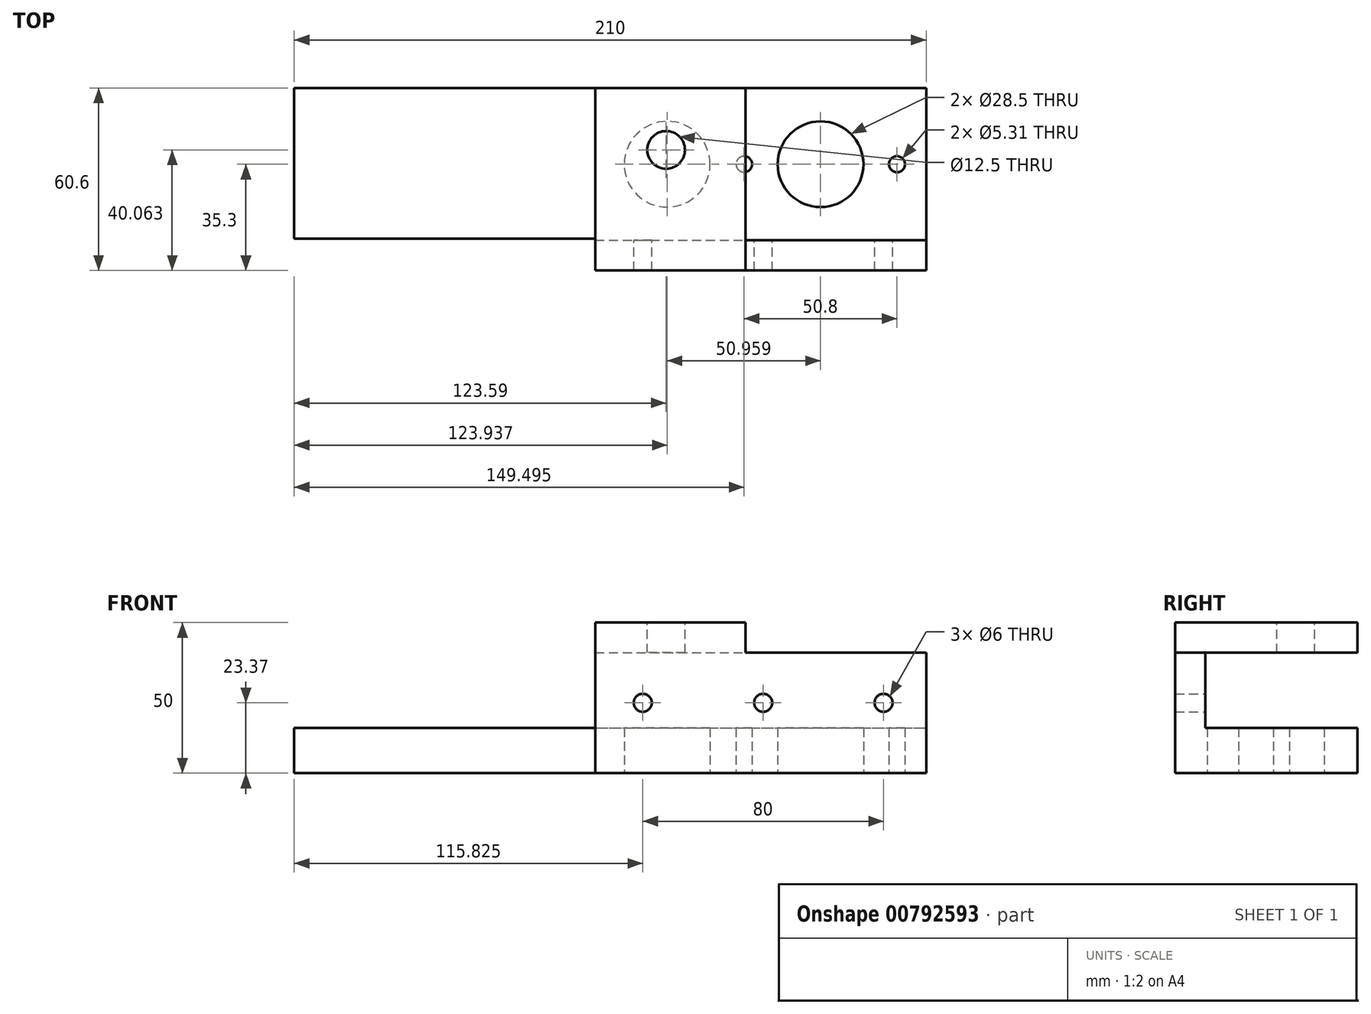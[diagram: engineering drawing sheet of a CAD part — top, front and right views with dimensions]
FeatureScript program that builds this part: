
annotation { "Feature Type Name" : "Feature", "Feature Type Description" : "" }
export const myFeature = defineFeature(function(context is Context, id is Id, definition is map)
    precondition{}
    {
        {
            var Q0;
            Q0=qCreatedBy(makeId("Top.planeOp"),FACE);
            var sketch = newSketch(context, id + "F0", { "sketchPlane" : qUnion([Q0])});
            skLineSegment(sketch, "E0.bottom", {"start": v(0, 0) * mm, "end": v(110, 0) * mm});
            skLineSegment(sketch, "E0.top", {"start": v(0, -50.6) * mm, "end": v(110, -50.6) * mm});
            skLineSegment(sketch, "E0.left", {"start": v(0, 0) * mm, "end": v(0, -50.6) * mm});
            skLineSegment(sketch, "E0.right", {"start": v(110, 0) * mm, "end": v(110, -50.6) * mm});
            skCircle(sketch, "E1", {"center": v(23.94, -25.3) * mm, "radius": 14.25 * mm});
            skPoint(sketch, "E1.centerSnap0", {"position": v(0, -25.3) * mm});
            skCircle(sketch, "E2", {"center": v(74.9, -25.3) * mm, "radius": 14.25 * mm});
            skLineSegment(sketch, "E3", {"start": v(74.9, -25.3) * mm, "end": v(100.3, -25.3) * mm, "construction": true});
            skCircle(sketch, "E4", {"center": v(100.3, -25.3) * mm, "radius": 2.66 * mm});
            skLineSegment(sketch, "E5", {"start": v(74.9, -11.05) * mm, "end": v(74.9, -21.34) * mm, "construction": true});
            skCircle(sketch, "E6.MirrorC", {"center": v(49.5, -25.3) * mm, "radius": 2.66 * mm});
            skLineSegment(sketch, "E7", {"start": v(74.9, -25.3) * mm, "end": v(74.9, -50.7) * mm, "construction": true});
            skSolve(sketch);
        }
        {
            var Q0;
            Q0 = qSketchRegion(id + "F0", true);
            extrude(context, id + "F1", {"entities" : qUnion([Q0]), "depth" : 15 * mm, "offsetDistance" : 25 * mm});
        }
        {
            var Q0;
            Q0=makeQuery(id+"F1.opExtrude","SWEPT_FACE",FACE,{"disambiguationData":[OSD([sQuery(id+"F0.wireOp",EDGE,"E0.top")])]});
            var sketch = newSketch(context, id + "F2", { "sketchPlane" : qUnion([Q0])});
            skLineSegment(sketch, "E8.bottom", {"start": v(0, 0) * mm, "end": v(110, 0) * mm});
            skLineSegment(sketch, "E8.top", {"start": v(0, 40) * mm, "end": v(110, 40) * mm});
            skLineSegment(sketch, "E8.left", {"start": v(0, 0) * mm, "end": v(0, 40) * mm});
            skLineSegment(sketch, "E8.right", {"start": v(110, 0) * mm, "end": v(110, 40) * mm});
            skSolve(sketch);
        }
        {
            var Q0;
            Q0 = qSketchRegion(id + "F2", true);
            extrude(context, id + "F3", {"entities" : qUnion([Q0]), "operationType" : NewBodyOperationType.ADD, "depth" : 10 * mm, "offsetDistance" : 25 * mm});
        }
        {
            var Q0;
            Q0=makeQuery(id+"F3.opExtrude","CAP_FACE",FACE,{"disambiguationData":[OSD([sQuery(id+"F2.wireOp",EDGE,"E8.bottom"),sQuery(id+"F2.wireOp",EDGE,"E8.top"),sQuery(id+"F2.wireOp",EDGE,"E8.left"),sQuery(id+"F2.wireOp",EDGE,"E8.right")])],"isStart":true});
            var sketch = newSketch(context, id + "F4", { "sketchPlane" : qUnion([Q0])});
            skCircle(sketch, "E9", {"center": v(-95.83, 23.37) * mm, "radius": 3 * mm});
            skCircle(sketch, "E10.1.0.0", {"center": v(-55.83, 23.37) * mm, "radius": 3 * mm});
            skCircle(sketch, "E10.2.0.0", {"center": v(-15.83, 23.37) * mm, "radius": 3 * mm});
            skLineSegment(sketch, "E10.direction1", {"start": v(-95.83, 23.37) * mm, "end": v(-55.83, 23.37) * mm, "construction": true});
            skSolve(sketch);
        }
        {
            var Q0;
            Q0 = qSketchRegion(id + "F4", true);
            extrude(context, id + "F5", {"entities" : qUnion([Q0]), "operationType" : NewBodyOperationType.REMOVE, "oppositeDirection" : true, "depth" : 25 * mm, "offsetDistance" : 25 * mm});
        }
        {
            var Q0;
            Q0=makeQuery(id+"F3.opExtrude","SWEPT_FACE",FACE,{"disambiguationData":[OSD([sQuery(id+"F2.wireOp",EDGE,"E8.top")])]});
            var sketch = newSketch(context, id + "F6", { "sketchPlane" : qUnion([Q0])});
            skLineSegment(sketch, "E11.bottom", {"start": v(0, -60.6) * mm, "end": v(50, -60.6) * mm});
            skLineSegment(sketch, "E11.top", {"start": v(0, 0) * mm, "end": v(50, 0) * mm});
            skLineSegment(sketch, "E11.left", {"start": v(0, -60.6) * mm, "end": v(0, 0) * mm});
            skLineSegment(sketch, "E11.right", {"start": v(50, -60.6) * mm, "end": v(50, 0) * mm});
            skSolve(sketch);
        }
        {
            var Q0;
            Q0 = qSketchRegion(id + "F6", true);
            extrude(context, id + "F7", {"entities" : qUnion([Q0]), "operationType" : NewBodyOperationType.ADD, "depth" : 10 * mm, "offsetDistance" : 25 * mm});
        }
        {
            var Q0;
            Q0=makeQuery(id+"F7.opExtrude","CAP_FACE",FACE,{"disambiguationData":[OSD([sQuery(id+"F6.wireOp",EDGE,"E11.bottom"),sQuery(id+"F6.wireOp",EDGE,"E11.top"),sQuery(id+"F6.wireOp",EDGE,"E11.left"),sQuery(id+"F6.wireOp",EDGE,"E11.right")])],"isStart":false});
            var sketch = newSketch(context, id + "F8", { "sketchPlane" : qUnion([Q0])});
            skCircle(sketch, "E12", {"center": v(23.6, -20.54) * mm, "radius": 6.25 * mm});
            skSolve(sketch);
        }
        {
            var Q0;
            Q0 = qSketchRegion(id + "F8", true);
            extrude(context, id + "F9", {"entities" : qUnion([Q0]), "operationType" : NewBodyOperationType.REMOVE, "oppositeDirection" : true, "depth" : 25 * mm, "offsetDistance" : 25 * mm});
        }
        {
            var Q0;
            Q0=makeQuery(id+"F7.boolean.opBoolean","MERGE",FACE,{"derivedFrom":[makeQuery(id+"F3.boolean.opBoolean","MERGE",FACE,{"derivedFrom":[makeQuery(id+"F1.opExtrude","SWEPT_FACE",FACE,{"disambiguationData":[OSD([sQuery(id+"F0.wireOp",EDGE,"E0.left")])]}),makeQuery(id+"F3.opExtrude","SWEPT_FACE",FACE,{"disambiguationData":[OSD([sQuery(id+"F2.wireOp",EDGE,"E8.left")])]})]}),makeQuery(id+"F7.opExtrude","SWEPT_FACE",FACE,{"disambiguationData":[OSD([sQuery(id+"F6.wireOp",EDGE,"E11.left")])]})]});
            var sketch = newSketch(context, id + "F10", { "sketchPlane" : qUnion([Q0])});
            skSolve(sketch);
        }
        {
            var Q0;
            Q0=qCreatedBy(makeId("Top.planeOp"),FACE);
            var sketch = newSketch(context, id + "F11", { "sketchPlane" : qUnion([Q0])});
            skLineSegment(sketch, "E13.bottom", {"start": v(0, -50) * mm, "end": v(-100, -50) * mm});
            skLineSegment(sketch, "E13.top", {"start": v(0, 0) * mm, "end": v(-100, 0) * mm});
            skLineSegment(sketch, "E13.left", {"start": v(0, -50) * mm, "end": v(0, 0) * mm});
            skLineSegment(sketch, "E13.right", {"start": v(-100, -50) * mm, "end": v(-100, 0) * mm});
            skSolve(sketch);
        }
        {
            var Q0;
            Q0 = qSketchRegion(id + "F11", true);
            extrude(context, id + "F12", {"entities" : qUnion([Q0]), "operationType" : NewBodyOperationType.ADD, "depth" : 15 * mm, "offsetDistance" : 25 * mm});
        }
    });
